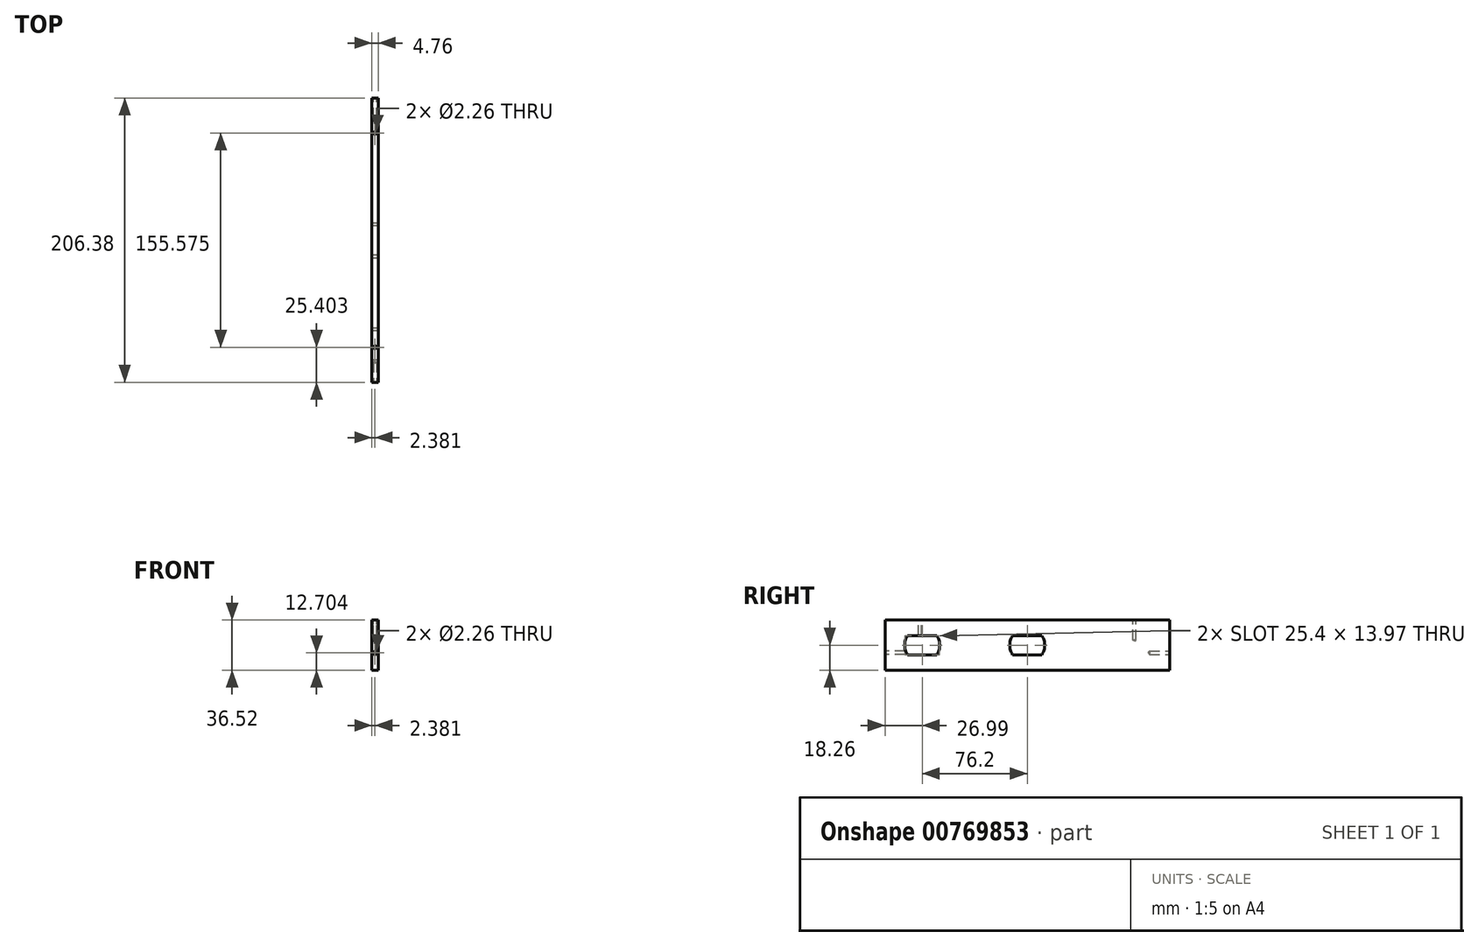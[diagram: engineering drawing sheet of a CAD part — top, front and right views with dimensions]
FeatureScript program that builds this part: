
annotation { "Feature Type Name" : "Feature", "Feature Type Description" : "" }
export const myFeature = defineFeature(function(context is Context, id is Id, definition is map)
    precondition{}
    {
        {
            var Q0;
            Q0=qCreatedBy(makeId("Right.planeOp"),FACE);
            var sketch = newSketch(context, id + "F0", { "sketchPlane" : qUnion([Q0])});
            skLineSegment(sketch, "E0.bottom", {"start": v(-103.19, 18.26) * mm, "end": v(103.19, 18.26) * mm});
            skLineSegment(sketch, "E0.top", {"start": v(-103.19, -18.26) * mm, "end": v(103.19, -18.26) * mm});
            skLineSegment(sketch, "E0.left", {"start": v(-103.19, 18.26) * mm, "end": v(-103.19, -18.26) * mm});
            skLineSegment(sketch, "E0.right", {"start": v(103.19, 18.26) * mm, "end": v(103.19, -18.26) * mm});
            skLineSegment(sketch, "E1", {"start": v(-103.19, 18.26) * mm, "end": v(103.19, -18.26) * mm, "construction": true});
            skSolve(sketch);
        }
        {
            var Q0;
            Q0 = qSketchRegion(id + "F0", true);
            extrude(context, id + "F1", {"entities" : qUnion([Q0]), "depth" : 4.76 * mm, "offsetDistance" : 25.4 * mm});
        }
        {
            var Q0;
            Q0=makeQuery(id+"F1.opExtrude","SWEPT_FACE",FACE,{"disambiguationData":[OSD([sQuery(id+"F0.wireOp",EDGE,"E0.right")])]});
            var sketch = newSketch(context, id + "F2", { "sketchPlane" : qUnion([Q0])});
            skLineSegment(sketch, "E2", {"start": v(-2.38, 18.26) * mm, "end": v(-2.38, -18.26) * mm});
            skPoint(sketch, "E3", {"position": v(-2.38, -5.56) * mm});
            skSolve(sketch);
        }
        {
            var Q0;
            Q0=makeQuery(id+"F1.opExtrude","SWEPT_FACE",FACE,{"disambiguationData":[OSD([sQuery(id+"F0.wireOp",EDGE,"E0.left")])]});
            var sketch = newSketch(context, id + "F3", { "sketchPlane" : qUnion([Q0])});
            skLineSegment(sketch, "E4", {"start": v(2.38, 18.26) * mm, "end": v(2.38, -18.26) * mm, "construction": true});
            skPoint(sketch, "E5", {"position": v(2.38, -5.56) * mm});
            skSolve(sketch);
        }
        {
            var Q0;
            Q0=makeQuery(id+"F1.opExtrude","SWEPT_FACE",FACE,{"disambiguationData":[OSD([sQuery(id+"F0.wireOp",EDGE,"E0.bottom")])]});
            var sketch = newSketch(context, id + "F4", { "sketchPlane" : qUnion([Q0])});
            skLineSegment(sketch, "E6", {"start": v(2.38, 103.19) * mm, "end": v(2.38, -103.19) * mm, "construction": true});
            skPoint(sketch, "E7", {"position": v(2.38, 77.79) * mm});
            skPoint(sketch, "E8", {"position": v(2.38, -77.79) * mm});
            skSolve(sketch);
        }
        {
            var Q0;
            Q0=sQuery(id+"F4.wireOp",VERTEX,"E8");
            var Q1;
            Q1=sQuery(id+"F3.wireOp",VERTEX,"E5");
            var Q2;
            Q2=sQuery(id+"F4.wireOp",VERTEX,"E7");
            var Q3;
            Q3=sQuery(id+"F2.wireOp",VERTEX,"E3");
            var Q4;
            Q4=makeQuery(id+"F1.opExtrude","SWEPT_BODY",BODY,{"disambiguationData":[OSD([sQuery(id+"F0.wireOp",EDGE,"E0.bottom"),sQuery(id+"F0.wireOp",EDGE,"E0.top"),sQuery(id+"F0.wireOp",EDGE,"E0.left"),sQuery(id+"F0.wireOp",EDGE,"E0.right")])]});
            hole(context, id + "F5", {"style" : HoleStyle.SIMPLE, "endStyle" : HoleEndStyle.BLIND, "standardTappedOrClearance" : lookupTablePath({ "standard" : "ANSI", "engagement" : "75%", "pitch" : "40 tpi", "size" : "#4", "type" : "Tapped" }), "standardBlindInLast" : lookupTablePath({ "standard" : "ANSI", "engagement" : "75%", "pitch" : "40 tpi", "size" : "#4", "type" : "Tapped" }), "holeDiameter" : 2.26 * mm, "majorDiameter" : 2.84 * mm, "showTappedDepth" : true, "holeDepth" : 14.6 * mm, "tappedDepth" : 12.7 * mm, "tapClearance" : 3, "locations" : qUnion([Q0, Q1, Q2, Q3]), "scope" : qUnion([Q4])});
        }
        {
            var Q0;
            Q0=makeQuery(id+"F1.opExtrude","CAP_FACE",FACE,{"disambiguationData":[OSD([sQuery(id+"F0.wireOp",EDGE,"E0.bottom"),sQuery(id+"F0.wireOp",EDGE,"E0.top"),sQuery(id+"F0.wireOp",EDGE,"E0.left"),sQuery(id+"F0.wireOp",EDGE,"E0.right")])],"isStart":false});
            var sketch = newSketch(context, id + "F6", { "sketchPlane" : qUnion([Q0])});
            skLineSegment(sketch, "E9", {"start": v(-103.19, 0) * mm, "end": v(103.19, 0) * mm, "construction": true});
            skLineSegment(sketch, "E10", {"start": v(0, 18.26) * mm, "end": v(0, -18.26) * mm, "construction": true});
            skArc(sketch, "E11", {"start": v(-86.8, 6.98) * mm, "mid": v(-88.9, 0) * mm, "end": v(-86.8, -6.99) * mm});
            skLineSegment(sketch, "E12.bottom", {"start": v(-86.8, 6.99) * mm, "end": v(-65.6, 6.99) * mm});
            skLineSegment(sketch, "E12.top", {"start": v(-86.8, -6.99) * mm, "end": v(-65.6, -6.99) * mm});
            skLineSegment(sketch, "E12.left", {"start": v(-86.8, 6.99) * mm, "end": v(-86.8, -6.99) * mm, "construction": true});
            skLineSegment(sketch, "E12.right", {"start": v(-65.6, 6.99) * mm, "end": v(-65.6, -6.99) * mm, "construction": true});
            skArc(sketch, "E13.trimOffspring", {"start": v(-65.6, -6.99) * mm, "mid": v(-63.5, 0) * mm, "end": v(-65.6, 6.98) * mm});
            skArc(sketch, "E14.MirrorCS", {"start": v(10.6, 6.98) * mm, "mid": v(12.7, 0) * mm, "end": v(10.6, -6.99) * mm});
            skLineSegment(sketch, "E15.MirrorCS", {"start": v(10.6, 6.98) * mm, "end": v(-10.6, 6.98) * mm});
            skArc(sketch, "E16.MirrorCS", {"start": v(-10.6, -6.99) * mm, "mid": v(-12.7, 0) * mm, "end": v(-10.6, 6.98) * mm});
            skLineSegment(sketch, "E17", {"start": v(10.6, -6.99) * mm, "end": v(-10.6, -6.99) * mm});
            skLineSegment(sketch, "E18", {"start": v(10.6, 6.98) * mm, "end": v(10.6, -6.99) * mm, "construction": true});
            skLineSegment(sketch, "E19", {"start": v(-10.6, 6.98) * mm, "end": v(-10.6, -6.99) * mm, "construction": true});
            skCircle(sketch, "E20", {"center": v(0, 0) * mm, "radius": 12.7 * mm, "construction": true});
            skSolve(sketch);
        }
        {
            var Q0;
            Q0 = qSketchRegion(id + "F6", true);
            extrude(context, id + "F7", {"entities" : qUnion([Q0]), "operationType" : NewBodyOperationType.REMOVE, "oppositeDirection" : true, "depth" : 25.4 * mm, "offsetDistance" : 25.4 * mm});
        }
    });
